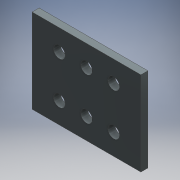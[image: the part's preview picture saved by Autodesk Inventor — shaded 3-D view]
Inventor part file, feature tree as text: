
AUTODESK INVENTOR PART (.ipt)
format: ipt  version: 2016 (Build 200138000, 138)  size: 130,560 bytes
history: native  units: mm
features: extrude x1, sketch x1
ambient origin geometry x8: Origin, YZ Plane, XZ Plane, XY Plane, X Axis, Y Axis, Z Axis, Center Point
bodies: Body1 (feature_tree)
feature tree (2):
  extrude  "Extrusion6"  Depth=36.0mm
  sketch  "Sketch1"  dims[d0=46.5mm d1=36.0mm d2=5.0mm d3=11.625mm d4=27.0mm d6=5.0mm d7=11.625mm d13=5.0mm d15=11.625mm d47=3.0mm d48=0.0mm]
